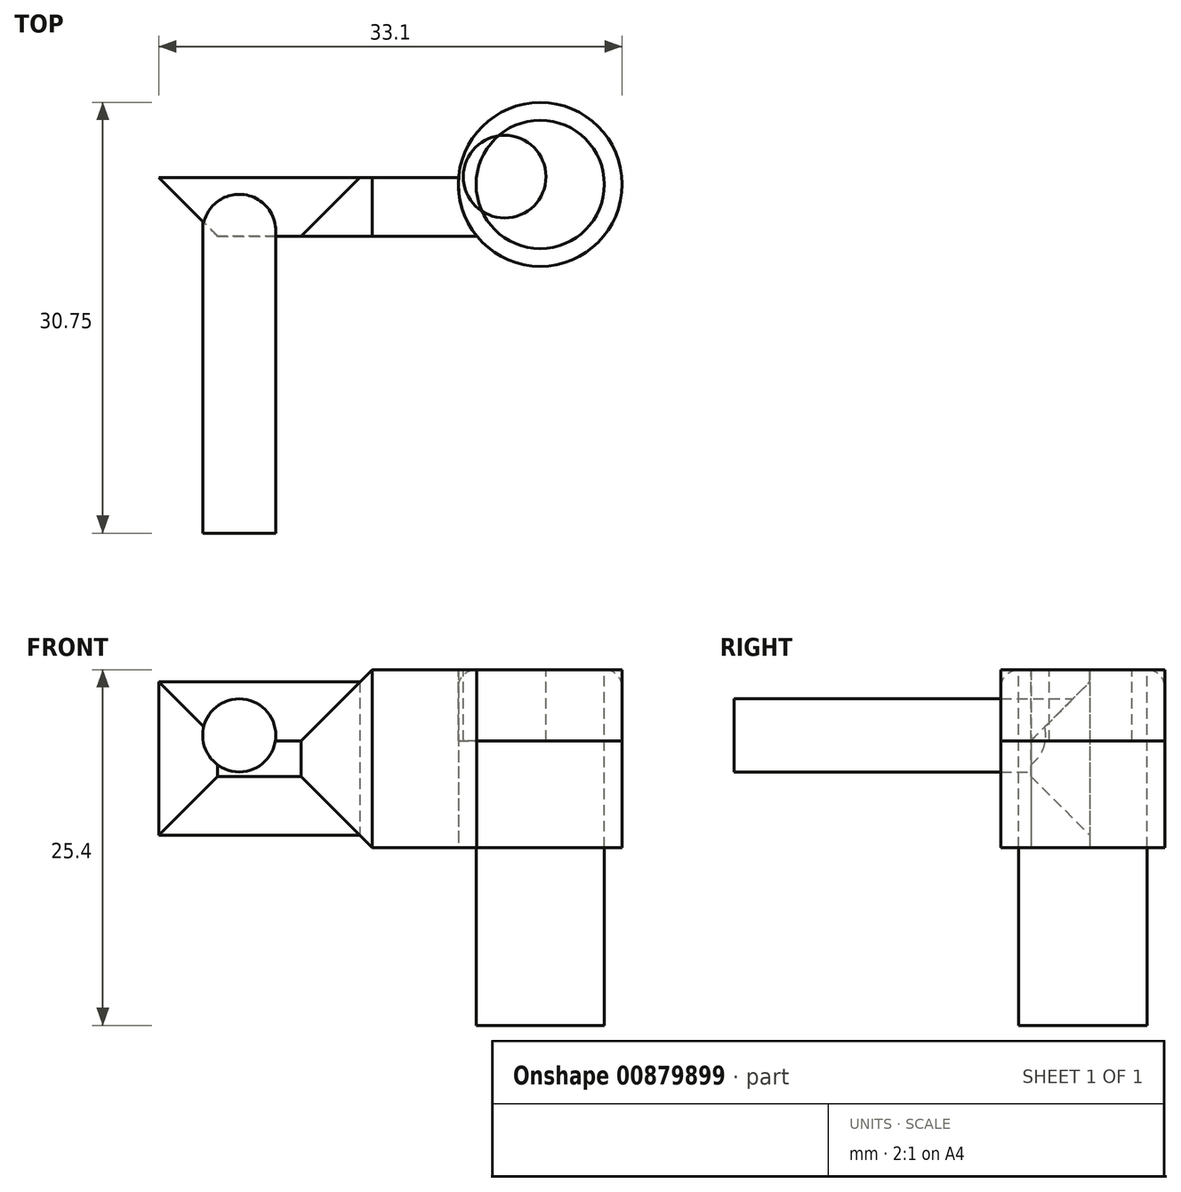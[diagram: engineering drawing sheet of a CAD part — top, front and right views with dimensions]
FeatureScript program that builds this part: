
annotation { "Feature Type Name" : "Feature", "Feature Type Description" : "" }
export const myFeature = defineFeature(function(context is Context, id is Id, definition is map)
    precondition{}
    {
        {
            var Q0;
            Q0=qCreatedBy(makeId("Top.planeOp"),FACE);
            var sketch = newSketch(context, id + "F0", { "sketchPlane" : qUnion([Q0])});
            skLineSegment(sketch, "E0.bottom", {"start": v(7.88, -39.44) * mm, "end": v(23.99, -39.44) * mm});
            skLineSegment(sketch, "E0.top", {"start": v(7.88, -43.65) * mm, "end": v(23.99, -43.65) * mm});
            skLineSegment(sketch, "E0.left", {"start": v(7.88, -39.44) * mm, "end": v(7.88, -43.65) * mm});
            skLineSegment(sketch, "E0.right", {"start": v(23.99, -39.44) * mm, "end": v(23.99, -43.65) * mm});
            skLineSegment(sketch, "E1.bottom", {"start": v(23.99, -18.12) * mm, "end": v(23.99, -18.12) * mm});
            skLineSegment(sketch, "E1.top", {"start": v(23.99, -28.17) * mm, "end": v(23.99, -28.17) * mm});
            skLineSegment(sketch, "E1.left", {"start": v(23.99, -18.12) * mm, "end": v(23.99, -28.17) * mm});
            skLineSegment(sketch, "E1.right", {"start": v(23.99, -18.12) * mm, "end": v(23.99, -28.17) * mm});
            skSolve(sketch);
        }
        {
            var Q0;
            Q0 = qSketchRegion(id + "F0", true);
            extrude(context, id + "F1", {"entities" : qUnion([Q0]), "depth" : 12.7 * mm, "offsetDistance" : 25.4 * mm});
        }
        {
            var Q0;
            Q0=qCreatedBy(makeId("Top.planeOp"),FACE);
            var sketch = newSketch(context, id + "F2", { "sketchPlane" : qUnion([Q0])});
            skCircle(sketch, "E2", {"center": v(36, -39.94) * mm, "radius": 5.85 * mm});
            skSolve(sketch);
        }
        {
            var Q0;
            Q0 = qSketchRegion(id + "F2", true);
            extrude(context, id + "F3", {"entities" : qUnion([Q0]), "depth" : 12.7 * mm, "offsetDistance" : 25.4 * mm});
        }
        {
            var Q0;
            Q0=makeQuery(id+"F1.opExtrude","SWEPT_FACE",FACE,{"disambiguationData":[OSD([sQuery(id+"F0.wireOp",EDGE,"E0.right")])]});
            extrude(context, id + "F4", {"entities" : qUnion([Q0]), "endBound" : BoundingType.UP_TO_NEXT, "depth" : 25.4 * mm, "offsetDistance" : 25.4 * mm});
        }
        {
            var Q0;
            Q0=makeQuery(id+"F3.opExtrude","CAP_FACE",FACE,{"disambiguationData":[OSD([sQuery(id+"F2.wireOp",EDGE,"E2")])],"isStart":false});
            var sketch = newSketch(context, id + "F5", { "sketchPlane" : qUnion([Q0])});
            skCircle(sketch, "E3", {"center": v(33.46, -39.39) * mm, "radius": 2.95 * mm});
            skSolve(sketch);
        }
        {
            var Q0;
            Q0=makeQuery(id+"F1.opExtrude","SWEPT_FACE",FACE,{"disambiguationData":[OSD([sQuery(id+"F0.wireOp",EDGE,"E0.top")])]});
            chamfer(context, id + "F6", {"entities" : qUnion([Q0]), "width" : 5.08 * mm, "tangentPropagation" : true});
        }
        {
            var Q0;
            Q0=makeQuery(id+"F3.opExtrude","CAP_FACE",FACE,{"disambiguationData":[OSD([sQuery(id+"F2.wireOp",EDGE,"E2")])],"isStart":false});
            fillet(context, id + "F7", {"entities" : qUnion([Q0]), "radius" : 1.27 * mm, "tangentPropagation" : true, "allowEdgeOverflow" : false});
        }
        {
            var Q0;
            Q0=makeQuery(id+"F5.imprint","IMPRINT",FACE,{"disambiguationData":[TD([[makeQuery(id+"F5.imprint","IMPRINT",EDGE,{"derivedFrom":sQuery(id+"F5.wireOp",EDGE,"E3")}),-1.0]])]});
            extrude(context, id + "F8", {"entities" : qUnion([Q0]), "depth" : -5.08 * mm, "offsetDistance" : 25.4 * mm});
        }
        {
            var Q0;
            Q0=makeQuery(id+"F6.opChamfer","BLEND_FACE",FACE,{"disambiguationData":[OSD([sQuery(id+"F0.wireOp",EDGE,"E0.top"),sQuery(id+"F0.wireOp",EDGE,"E0.right")])]});
            var Q1;
            Q1=makeQuery(id+"F4.opExtrude","CAP_EDGE",EDGE,{"disambiguationData":[OSD([sQuery(id+"F0.wireOp",EDGE,"E0.bottom"),sQuery(id+"F0.wireOp",EDGE,"E0.right")])],"isStart":true});
            var Q2;
            Q2=makeQuery(id+"F6.opChamfer","BLEND_EDGE",EDGE,{"blendedFrom":[makeQuery(id+"F1.opExtrude","SWEPT_EDGE",EDGE,{"disambiguationData":[OSD([sQuery(id+"F0.wireOp",EDGE,"E0.top"),sQuery(id+"F0.wireOp",EDGE,"E0.right")])]}),makeQuery(id+"F1.opExtrude","SWEPT_FACE",FACE,{"disambiguationData":[OSD([sQuery(id+"F0.wireOp",EDGE,"E0.bottom")])]})],"blendedInto":[makeQuery(id+"F1.opExtrude","SWEPT_FACE",FACE,{"disambiguationData":[OSD([sQuery(id+"F0.wireOp",EDGE,"E0.bottom")])]})]});
            loft(context, id + "F9", {"bodyType" : ToolBodyType.SURFACE, "sheetProfilesArray" : [{ "sheetProfileEntities" : qUnion([Q0]) }], "wireProfilesArray" : [{ "wireProfileEntities" : qUnion([Q1]) }, { "wireProfileEntities" : qUnion([Q2]) }]});
        }
        {
            var Q0;
            Q0=makeQuery(id+"F6.opChamfer","BLEND_FACE",FACE,{"disambiguationData":[OSD([sQuery(id+"F0.wireOp",EDGE,"E0.top"),sQuery(id+"F0.wireOp",EDGE,"E0.right")])]});
            var Q1;
            Q1=makeQuery(id+"F4.opExtrude","CAP_FACE",FACE,{"disambiguationData":[OSD([sQuery(id+"F0.wireOp",EDGE,"E0.right")])],"isStart":true});
            loft(context, id + "F10", {"sheetProfilesArray" : [{ "sheetProfileEntities" : qUnion([Q0]) }, { "sheetProfileEntities" : qUnion([Q1]) }]});
        }
        {
            var Q0;
            Q0=makeQuery(id+"F3.opExtrude","CAP_FACE",FACE,{"disambiguationData":[OSD([sQuery(id+"F2.wireOp",EDGE,"E2")])],"isStart":false});
            extrude(context, id + "F11", {"entities" : qUnion([Q0]), "oppositeDirection" : true, "depth" : 25.4 * mm, "offsetDistance" : 25.4 * mm});
        }
        {
            var Q0;
            Q0=makeQuery(id+"F1.opExtrude","SWEPT_FACE",FACE,{"disambiguationData":[OSD([sQuery(id+"F0.wireOp",EDGE,"E0.bottom")])]});
            var sketch = newSketch(context, id + "F12", { "sketchPlane" : qUnion([Q0])});
            skSolve(sketch);
        }
        {
            var Q0;
            {var subQ0=makeQuery(id+"F1.opExtrude","SWEPT_FACE",FACE,{"disambiguationData":[OSD([sQuery(id+"F0.wireOp",EDGE,"E0.bottom")])]});var subQ1=sQuery(id+"F0.wireOp",EDGE,"E0.top");Q0=makeQuery(id+"F12.imprint","IMPRINT",FACE,{"disambiguationData":[TD([[makeQuery(id+"F12.imprint","IMPRINT",EDGE,{"derivedFrom":makeQuery(id+"F6.opChamfer","BLEND_EDGE",EDGE,{"blendedFrom":[makeQuery(id+"F1.opExtrude","CAP_EDGE",EDGE,{"disambiguationData":[OSD([subQ1])],"isStart":true}),subQ0],"blendedInto":[subQ0]})}),1.0]])]});}
            var sketch = newSketch(context, id + "F13", { "sketchPlane" : qUnion([Q0])});
            skCircle(sketch, "E4", {"center": v(-14.5, 8) * mm, "radius": 2.61 * mm});
            skSolve(sketch);
        }
        {
            var Q0;
            Q0 = qSketchRegion(id + "F13", true);
            extrude(context, id + "F14", {"entities" : qUnion([Q0]), "operationType" : NewBodyOperationType.ADD, "oppositeDirection" : true, "depth" : 25.4 * mm, "offsetDistance" : 25.4 * mm});
        }
    });
